# Revit family: Domotics-DomesticRanges-GEWISS-CHORUS_DATA-CONNECTOR_2RCA
name_source: partatom
category: Apparecchi elettrici
revit_build: Autodesk Revit 2016 (Build: 20161004_0715(x64)
units: mm (PartAtom-declared; Revit-internal decimal feet)

## family parameters
Condiviso = Sì
Host = Superficie
Mantenere orientamento annotazione = Sì
Punto di calcolo locali = Sì
Quota connettore circolare = Usa diametro
Taglio con vuoti quando caricato = No
Tipo di parte = Normale

## types (3) — shared parameters
Catalogue = DOMOTICS
Catalogue Range = CHORUS - SERIE CIVILE
Category = Connector
Description. = Connector
Description: = Double RCA
Electrocod = 3720
IDF = bcebf5b7-2d41-49c0-b232-bd4499ad4c3d
IDT = 3bd35a5f-1ef9-4d50-bd9c-7bbb83a91f20
Immagine tipo = GW14453.jpg
No. Chorus modules: = 1
Produttore = GEWISS S.p.A.
Prospetto di default = 1219 mm
SEO = Socket outlet
Standard; = EN 60958-3
Technical sheet = https://www.gewiss.com
Tipo_ = CONNETTORE DOPPIO RCA : titanio
URL = https://www.gewiss.com
Version file RFA = 19.0
fronte = titanio
struttura = Default

## per-type parameters (varying)
| type | Colour | Descrizione | EAN code | Modello |
| GW14453 - CONNECTOR, DOUBLE RCA 1M CHORUS TITANIUM | Titanium | CONNECTOR, DOUBLE RCA 1M CHORUS TITANIUM | 8011564265172 | GW14453 |
| GW12453 - CONNECTOR DOUBLE RCA 1M CHORUS BLACK | Black | CONNECTOR DOUBLE RCA 1M CHORUS BLACK | 8011564269170 | GW12453 |
| GW10453 - CONNECTOR DOUBLE RCA 1M WHITE | White | CONNECTOR DOUBLE RCA 1M WHITE | 8011564259522 | GW10453 |

## geometry (parser evidence)
native form markers: Sweep x2
no freeform markers — native parametric forms only
